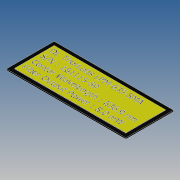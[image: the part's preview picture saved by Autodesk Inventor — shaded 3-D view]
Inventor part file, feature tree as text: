
AUTODESK INVENTOR PART (.ipt)
format: ipt  version: 2015 SP1 (Build 190203100, 203)  size: 1,833,984 bytes
history: native  units: mm
features: extrude x3, sketch x3, projected_geometry x2
ambient origin geometry x8: Origin, YZ Plane, XZ Plane, XY Plane, X Axis, Y Axis, Z Axis, Center Point
bodies: Solid1 (feature_tree)
feature tree (8):
  extrude  "Extrusion1"  Depth=12.0mm
  extrude  "Extrusion4"  Depth=0.1mm TaperAngle=0.0deg
  extrude  "Extrusion3"  Depth=1.0mm
  sketch  "Sketch1"  dims[d0=30.0mm d1=12.0mm]
  sketch  "Sketch2"  dims[d2=0.4mm d3=0.0mm d8=0.1mm d9=0.0mm]
  sketch  "Sketch3"  dims[d10=1.0mm d11=1.0mm d12=1.0mm d13=1.0mm d14=0.1mm d15=0.0mm]
  projected_geometry  "Project Cut Edges1"
  projected_geometry  "Project Cut Edges2"
